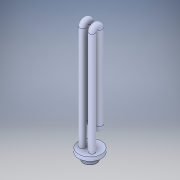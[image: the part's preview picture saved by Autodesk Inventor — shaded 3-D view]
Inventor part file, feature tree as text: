
AUTODESK INVENTOR PART (.ipt)
format: ipt  version: 2018 (Build 220112000, 112)  size: 156,160 bytes
history: native  units: in
note: dims shown in document units (in); Inventor stores cm internally (conversion verified against a paired STEP export)
features: extrude x1, chamfer x1, thread x1, sketch x1, projected_geometry x1, sweep x1
ambient origin geometry x8: Origin, YZ Plane, XZ Plane, XY Plane, X Axis, Y Axis, Z Axis, Center Point
bodies: Solid1 (feature_tree)
feature tree (6):
  extrude  "Extrusion1"  Depth=0.5in TaperAngle=0.0deg
  chamfer  "Chamfer1"  Distance=0.125in Angle=45.0deg
  thread  "Thread1"  [1 undecoded]
  sketch  "Sketch1"  dims[d0=1.0in d1=0.5in d2=0.0in d3=0.125in d4=0.0787in d5=45.0deg d6=0.3937in d7=0.0in]
  projected_geometry  "Projected Loop1"
  sweep  "Sweep4"
note: 1 required parameter value undecoded (feature->parameter linkage not recoverable at this tier; creation-order binding heuristic only, values carry confidence <= 0.55)
